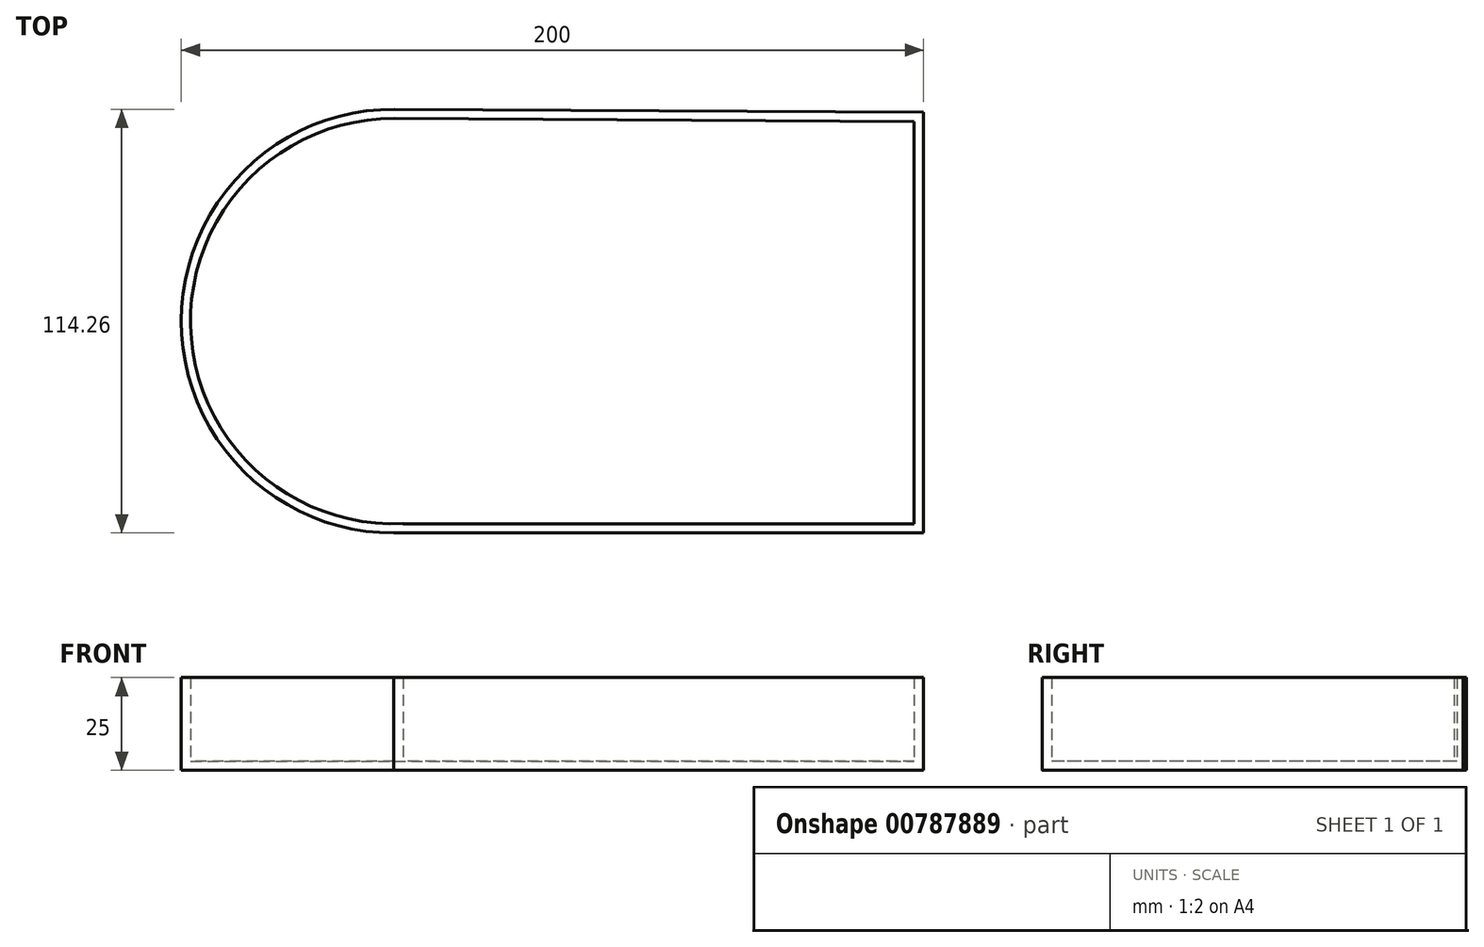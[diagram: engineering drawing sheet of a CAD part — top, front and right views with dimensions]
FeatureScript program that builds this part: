
annotation { "Feature Type Name" : "Feature", "Feature Type Description" : "" }
export const myFeature = defineFeature(function(context is Context, id is Id, definition is map)
    precondition{}
    {
        {
            var Q0;
            Q0=qCreatedBy(makeId("Top.planeOp"),FACE);
            var sketch = newSketch(context, id + "F0", { "sketchPlane" : qUnion([Q0])});
            skLineSegment(sketch, "E0.right", {"start": v(-48.75, -57.13) * mm, "end": v(-48.75, 57.13) * mm});
            skPoint(sketch, "E0.middle", {"position": v(0, 0) * mm});
            skCircle(sketch, "E1", {"center": v(-48.91, 0) * mm, "radius": 57.13 * mm});
            skLineSegment(sketch, "E2", {"start": v(-48.75, 57.13) * mm, "end": v(93.96, 56.3) * mm});
            skLineSegment(sketch, "E3", {"start": v(93.96, 56.3) * mm, "end": v(93.96, -57.11) * mm});
            skLineSegment(sketch, "E4", {"start": v(93.96, -57.11) * mm, "end": v(-48.75, -57.13) * mm});
            skSolve(sketch);
        }
        {
            var Q0;
            {var subQ0=sQuery(id+"F0.wireOp",EDGE,"E3");Q0=makeQuery(id+"F0.imprint","IMPRINT",FACE,{"disambiguationData":[TD([[makeQuery(id+"F0.imprint","IMPRINT",EDGE,{"derivedFrom":subQ0}),-1.0]])]});}
            var Q1;
            {var subQ0=sQuery(id+"F0.wireOp",EDGE,"E1");var subQ1=sQuery(id+"F0.wireOp",EDGE,"E0.right");var subQ2=makeQuery(id+"F0.imprint","INTERSECT",VERTEX,{"disambiguationData":[OD(0.0)],"derivedFrom":[subQ1,subQ0]});Q1=makeQuery(id+"F0.imprint","IMPRINT",FACE,{"disambiguationData":[TD([[makeQuery(id+"F0.imprint","IMPRINT",EDGE,{"disambiguationData":[TD([[subQ2,-1.0]])],"derivedFrom":subQ1}),-1.0]])]});}
            var Q2;
            {var subQ0=sQuery(id+"F0.wireOp",EDGE,"E1");var subQ1=sQuery(id+"F0.wireOp",EDGE,"E0.right");var subQ2=makeQuery(id+"F0.imprint","INTERSECT",VERTEX,{"disambiguationData":[OD(0.0)],"derivedFrom":[subQ1,subQ0]});Q2=makeQuery(id+"F0.imprint","IMPRINT",FACE,{"disambiguationData":[TD([[makeQuery(id+"F0.imprint","IMPRINT",EDGE,{"disambiguationData":[TD([[subQ2,-1.0]])],"derivedFrom":subQ1}),1.0]])]});}
            extrude(context, id + "F1", {"entities" : qUnion([Q0, Q1, Q2]), "endBound" : BoundingType.SYMMETRIC, "depth" : 25 * mm, "offsetDistance" : 25 * mm});
        }
        {
            var Q0;
            Q0=makeQuery(id+"F1.opExtrude","CAP_FACE",FACE,{"disambiguationData":[OSD([sQuery(id+"F0.wireOp",EDGE,"E0.right"),sQuery(id+"F0.wireOp",EDGE,"E1"),sQuery(id+"F0.wireOp",EDGE,"E2"),sQuery(id+"F0.wireOp",EDGE,"E3"),sQuery(id+"F0.wireOp",EDGE,"E4")])],"isStart":false});
            shell(context, id + "F2", {"entities" : qUnion([Q0]), "thickness" : 2.5 * mm});
        }
    });
